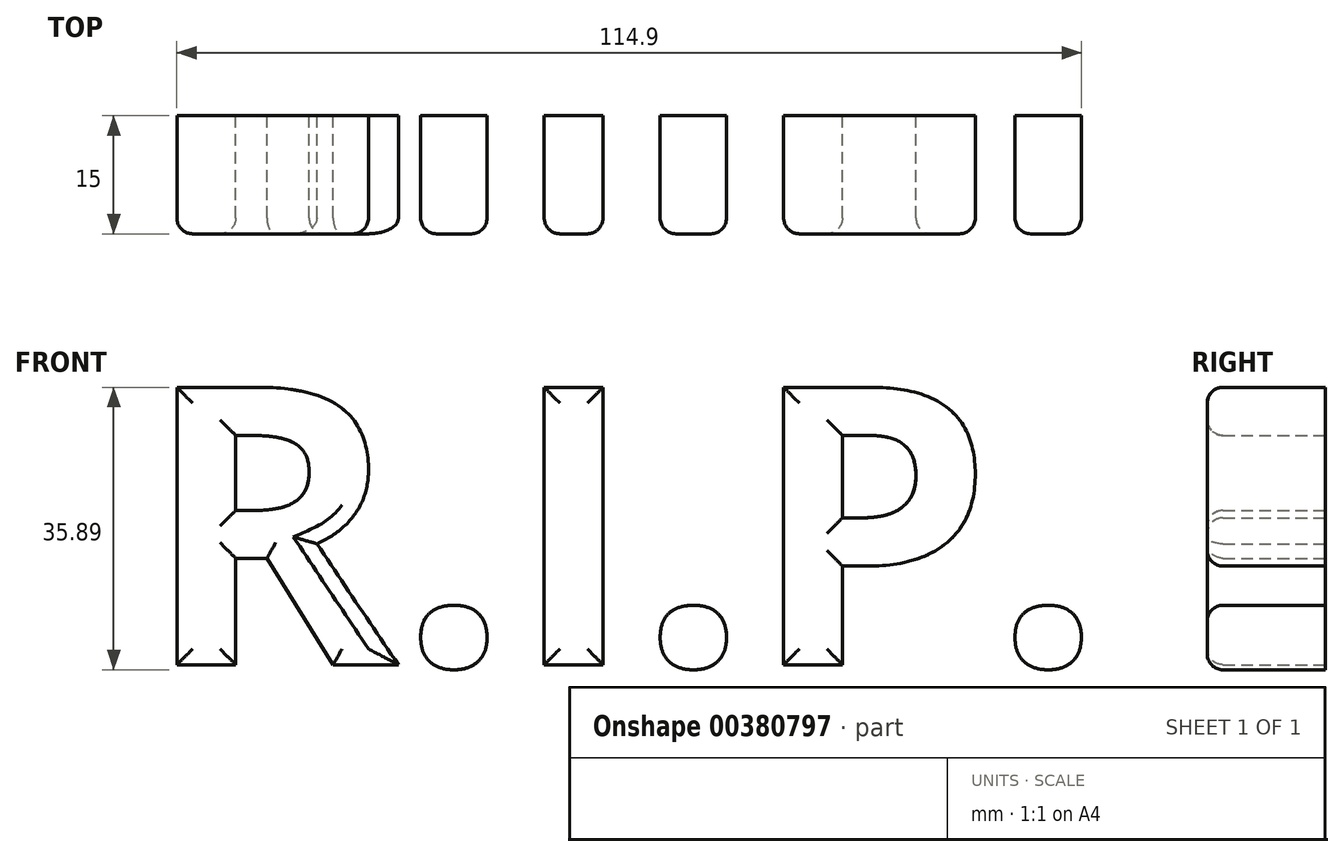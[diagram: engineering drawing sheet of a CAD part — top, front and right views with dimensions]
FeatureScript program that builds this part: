
annotation { "Feature Type Name" : "Feature", "Feature Type Description" : "" }
export const myFeature = defineFeature(function(context is Context, id is Id, definition is map)
    precondition{}
    {
        {
            var Q0;
            Q0=qCreatedBy(makeId("Front.planeOp"),FACE);
            var sketch = newSketch(context, id + "F0", { "sketchPlane" : qUnion([Q0])});
            skText(sketch, "E0", { "text": "R.I.P.", "fontName": "OpenSans-Bold.ttf"});
            const initialGuessF0  = {"E0": [-0.06144, 0.0047, 1, 0, 0.03554]};
            skSetInitialGuess(sketch, initialGuessF0);
            skSolve(sketch);
        }
        {
            var Q0;
            Q0 = qSketchRegion(id + "F0", true);
            extrude(context, id + "F1", {"entities" : qUnion([Q0]), "depth" : 15 * mm});
        }
        {
            var Q0;
            Q0=makeQuery(id+"F1.opExtrude","CAP_FACE",FACE,{"disambiguationData":[OSD([sQuery(id+"F0.wireOp",EDGE,"E0.sketch_text.stroke-0"),sQuery(id+"F0.wireOp",EDGE,"E0.sketch_text.stroke-1"),sQuery(id+"F0.wireOp",EDGE,"E0.sketch_text.stroke-2"),sQuery(id+"F0.wireOp",EDGE,"E0.sketch_text.stroke-3"),sQuery(id+"F0.wireOp",EDGE,"E0.sketch_text.stroke-4"),sQuery(id+"F0.wireOp",EDGE,"E0.sketch_text.stroke-5"),sQuery(id+"F0.wireOp",EDGE,"E0.sketch_text.stroke-6"),sQuery(id+"F0.wireOp",EDGE,"E0.sketch_text.stroke-7"),sQuery(id+"F0.wireOp",EDGE,"E0.sketch_text.stroke-8"),sQuery(id+"F0.wireOp",EDGE,"E0.sketch_text.stroke-9"),sQuery(id+"F0.wireOp",EDGE,"E0.sketch_text.stroke-10"),sQuery(id+"F0.wireOp",EDGE,"E0.sketch_text.stroke-11"),sQuery(id+"F0.wireOp",EDGE,"E0.sketch_text.stroke-12"),sQuery(id+"F0.wireOp",EDGE,"E0.sketch_text.stroke-13"),sQuery(id+"F0.wireOp",EDGE,"E0.sketch_text.stroke-14"),sQuery(id+"F0.wireOp",EDGE,"E0.sketch_text.stroke-15"),sQuery(id+"F0.wireOp",EDGE,"E0.sketch_text.stroke-16"),sQuery(id+"F0.wireOp",EDGE,"E0.sketch_text.stroke-17"),sQuery(id+"F0.wireOp",EDGE,"E0.sketch_text.stroke-18")])],"isStart":false});
            var Q1;
            Q1=makeQuery(id+"F1.opExtrude","CAP_FACE",FACE,{"disambiguationData":[OSD([sQuery(id+"F0.wireOp",EDGE,"E0.sketch_text.stroke-19"),sQuery(id+"F0.wireOp",EDGE,"E0.sketch_text.stroke-20"),sQuery(id+"F0.wireOp",EDGE,"E0.sketch_text.stroke-21"),sQuery(id+"F0.wireOp",EDGE,"E0.sketch_text.stroke-22"),sQuery(id+"F0.wireOp",EDGE,"E0.sketch_text.stroke-23"),sQuery(id+"F0.wireOp",EDGE,"E0.sketch_text.stroke-24"),sQuery(id+"F0.wireOp",EDGE,"E0.sketch_text.stroke-25"),sQuery(id+"F0.wireOp",EDGE,"E0.sketch_text.stroke-26")])],"isStart":false});
            var Q2;
            Q2=makeQuery(id+"F1.opExtrude","CAP_FACE",FACE,{"disambiguationData":[OSD([sQuery(id+"F0.wireOp",EDGE,"E0.sketch_text.stroke-27"),sQuery(id+"F0.wireOp",EDGE,"E0.sketch_text.stroke-28"),sQuery(id+"F0.wireOp",EDGE,"E0.sketch_text.stroke-29"),sQuery(id+"F0.wireOp",EDGE,"E0.sketch_text.stroke-30")])],"isStart":false});
            var Q3;
            Q3=makeQuery(id+"F1.opExtrude","CAP_FACE",FACE,{"disambiguationData":[OSD([sQuery(id+"F0.wireOp",EDGE,"E0.sketch_text.stroke-31"),sQuery(id+"F0.wireOp",EDGE,"E0.sketch_text.stroke-32"),sQuery(id+"F0.wireOp",EDGE,"E0.sketch_text.stroke-33"),sQuery(id+"F0.wireOp",EDGE,"E0.sketch_text.stroke-34"),sQuery(id+"F0.wireOp",EDGE,"E0.sketch_text.stroke-35"),sQuery(id+"F0.wireOp",EDGE,"E0.sketch_text.stroke-36"),sQuery(id+"F0.wireOp",EDGE,"E0.sketch_text.stroke-37"),sQuery(id+"F0.wireOp",EDGE,"E0.sketch_text.stroke-38")])],"isStart":false});
            var Q4;
            Q4=makeQuery(id+"F1.opExtrude","CAP_FACE",FACE,{"disambiguationData":[OSD([sQuery(id+"F0.wireOp",EDGE,"E0.sketch_text.stroke-39"),sQuery(id+"F0.wireOp",EDGE,"E0.sketch_text.stroke-40"),sQuery(id+"F0.wireOp",EDGE,"E0.sketch_text.stroke-41"),sQuery(id+"F0.wireOp",EDGE,"E0.sketch_text.stroke-42"),sQuery(id+"F0.wireOp",EDGE,"E0.sketch_text.stroke-43"),sQuery(id+"F0.wireOp",EDGE,"E0.sketch_text.stroke-44"),sQuery(id+"F0.wireOp",EDGE,"E0.sketch_text.stroke-45"),sQuery(id+"F0.wireOp",EDGE,"E0.sketch_text.stroke-46"),sQuery(id+"F0.wireOp",EDGE,"E0.sketch_text.stroke-47"),sQuery(id+"F0.wireOp",EDGE,"E0.sketch_text.stroke-48"),sQuery(id+"F0.wireOp",EDGE,"E0.sketch_text.stroke-49"),sQuery(id+"F0.wireOp",EDGE,"E0.sketch_text.stroke-50"),sQuery(id+"F0.wireOp",EDGE,"E0.sketch_text.stroke-51"),sQuery(id+"F0.wireOp",EDGE,"E0.sketch_text.stroke-52"),sQuery(id+"F0.wireOp",EDGE,"E0.sketch_text.stroke-53"),sQuery(id+"F0.wireOp",EDGE,"E0.sketch_text.stroke-54")])],"isStart":false});
            var Q5;
            Q5=makeQuery(id+"F1.opExtrude","CAP_FACE",FACE,{"disambiguationData":[OSD([sQuery(id+"F0.wireOp",EDGE,"E0.sketch_text.stroke-55"),sQuery(id+"F0.wireOp",EDGE,"E0.sketch_text.stroke-56"),sQuery(id+"F0.wireOp",EDGE,"E0.sketch_text.stroke-57"),sQuery(id+"F0.wireOp",EDGE,"E0.sketch_text.stroke-58"),sQuery(id+"F0.wireOp",EDGE,"E0.sketch_text.stroke-59"),sQuery(id+"F0.wireOp",EDGE,"E0.sketch_text.stroke-60"),sQuery(id+"F0.wireOp",EDGE,"E0.sketch_text.stroke-61"),sQuery(id+"F0.wireOp",EDGE,"E0.sketch_text.stroke-62")])],"isStart":false});
            fillet(context, id + "F2", {"entities" : qUnion([Q0, Q1, Q2, Q3, Q4, Q5]), "radius" : 2 * mm, "tangentPropagation" : true, "allowEdgeOverflow" : false});
        }
    });
